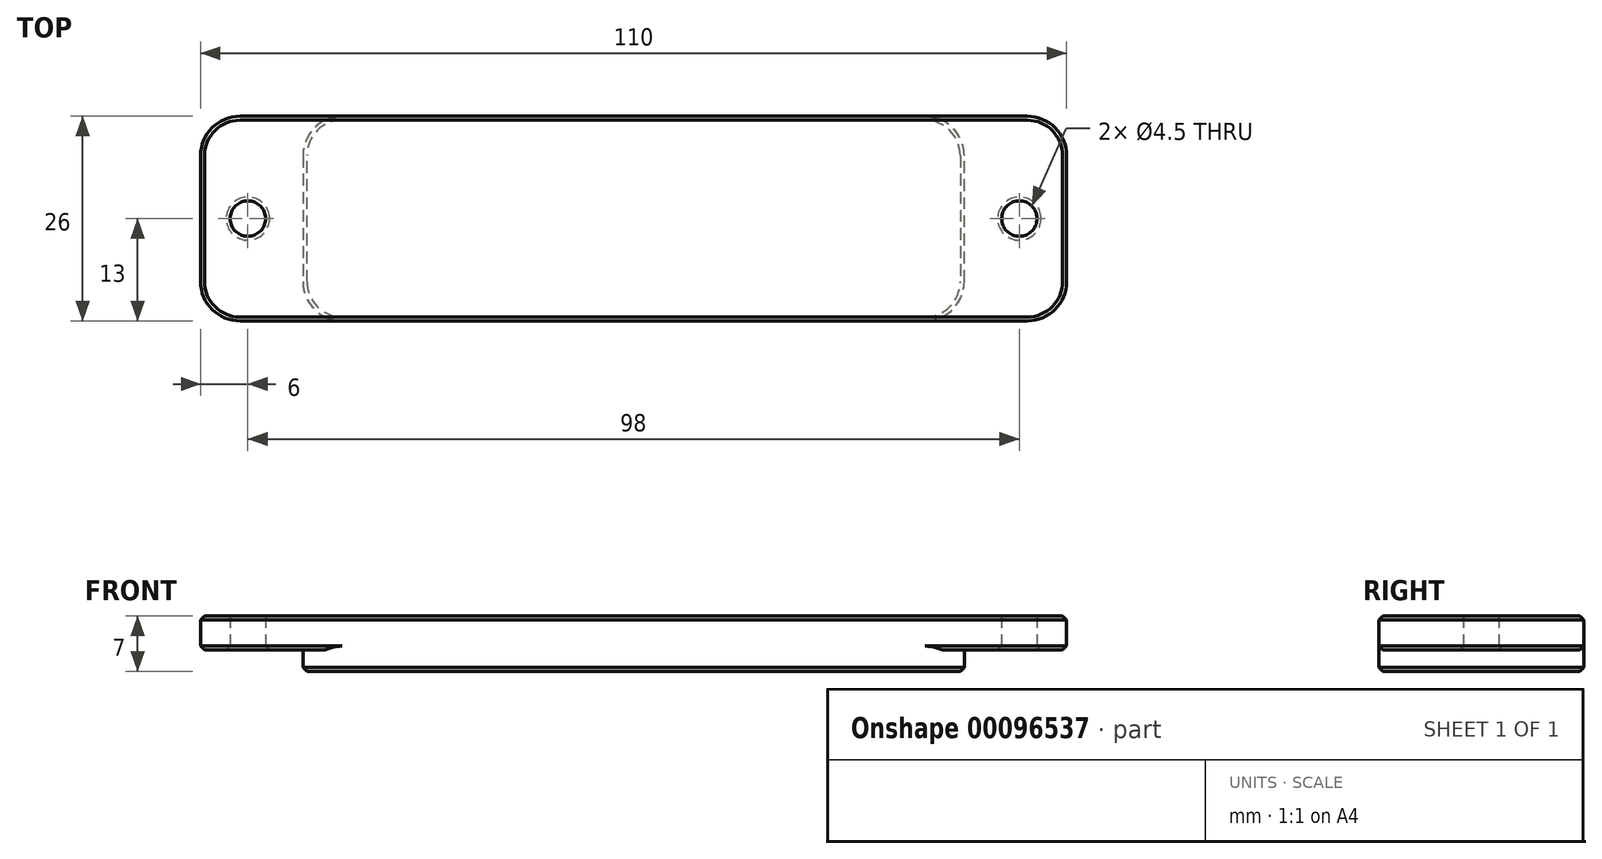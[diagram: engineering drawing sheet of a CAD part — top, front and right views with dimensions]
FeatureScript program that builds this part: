
annotation { "Feature Type Name" : "Feature", "Feature Type Description" : "" }
export const myFeature = defineFeature(function(context is Context, id is Id, definition is map)
    precondition{}
    {
        {
            var Q0;
            Q0=qCreatedBy(makeId("Top.planeOp"),FACE);
            var sketch = newSketch(context, id + "F0", { "sketchPlane" : qUnion([Q0])});
            skLineSegment(sketch, "E0.bottom", {"start": v(-37, 13) * mm, "end": v(37, 13) * mm});
            skLineSegment(sketch, "E0.top", {"start": v(-37, -13) * mm, "end": v(37, -13) * mm});
            skLineSegment(sketch, "E0.left", {"start": v(-42, 8) * mm, "end": v(-42, -8) * mm});
            skLineSegment(sketch, "E0.right", {"start": v(42, 8) * mm, "end": v(42, -8) * mm});
            skPoint(sketch, "E0.middle", {"position": v(0, 0) * mm});
            skPoint(sketch, "E1.visualSharp", {"position": v(-42, 13) * mm});
            skArc(sketch, "E1.filletArc", {"start": v(-37, 13) * mm, "mid": v(-40.54, 11.54) * mm, "end": v(-42, 8) * mm});
            skPoint(sketch, "E2.visualSharp", {"position": v(42, 13) * mm});
            skArc(sketch, "E2.filletArc", {"start": v(42, 8) * mm, "mid": v(40.54, 11.54) * mm, "end": v(37, 13) * mm});
            skPoint(sketch, "E3.visualSharp", {"position": v(42, -13) * mm});
            skArc(sketch, "E3.filletArc", {"start": v(37, -13) * mm, "mid": v(40.54, -11.54) * mm, "end": v(42, -8) * mm});
            skPoint(sketch, "E4.visualSharp", {"position": v(-42, -13) * mm});
            skArc(sketch, "E4.filletArc", {"start": v(-42, -8) * mm, "mid": v(-40.54, -11.54) * mm, "end": v(-37, -13) * mm});
            skSolve(sketch);
        }
        {
            var Q0;
            Q0 = qSketchRegion(id + "F0", true);
            extrude(context, id + "F1", {"entities" : qUnion([Q0]), "depth" : 2.7 * mm, "offsetDistance" : 25 * mm});
        }
        {
            var Q0;
            Q0=makeQuery(id+"F1.opExtrude","CAP_FACE",FACE,{"disambiguationData":[OSD([sQuery(id+"F0.wireOp",EDGE,"E0.bottom"),sQuery(id+"F0.wireOp",EDGE,"E0.top"),sQuery(id+"F0.wireOp",EDGE,"E0.left"),sQuery(id+"F0.wireOp",EDGE,"E0.right"),sQuery(id+"F0.wireOp",EDGE,"E1.filletArc"),sQuery(id+"F0.wireOp",EDGE,"E2.filletArc"),sQuery(id+"F0.wireOp",EDGE,"E3.filletArc"),sQuery(id+"F0.wireOp",EDGE,"E4.filletArc")])],"isStart":true});
            cPlane(context, id + "F2", {"entities" : qUnion([Q0]), "cplaneType" : CPlaneType.OFFSET, "offset" : 7 * mm, "oppositeDirection" : true, "width" : 150 * mm, "height" : 150 * mm});
        }
        {
            var Q0;
            Q0=makeQuery(id+"F1.opExtrude","CAP_FACE",FACE,{"disambiguationData":[OSD([sQuery(id+"F0.wireOp",EDGE,"E0.bottom"),sQuery(id+"F0.wireOp",EDGE,"E0.top"),sQuery(id+"F0.wireOp",EDGE,"E0.left"),sQuery(id+"F0.wireOp",EDGE,"E0.right"),sQuery(id+"F0.wireOp",EDGE,"E1.filletArc"),sQuery(id+"F0.wireOp",EDGE,"E2.filletArc"),sQuery(id+"F0.wireOp",EDGE,"E3.filletArc"),sQuery(id+"F0.wireOp",EDGE,"E4.filletArc")])],"isStart":false});
            var sketch = newSketch(context, id + "F3", { "sketchPlane" : qUnion([Q0])});
            skPoint(sketch, "E5.middle", {"position": v(0, 0) * mm});
            skPoint(sketch, "E6.orphan", {"position": v(-37, -13) * mm});
            skPoint(sketch, "E7.orphan", {"position": v(37, -13) * mm});
            skPoint(sketch, "E8.orphan", {"position": v(37, 13) * mm});
            skPoint(sketch, "E9.orphan", {"position": v(-37, 13) * mm});
            skLineSegment(sketch, "E10.bottom", {"start": v(-50, 13) * mm, "end": v(50, 13) * mm});
            skLineSegment(sketch, "E10.top", {"start": v(-50, -13) * mm, "end": v(50, -13) * mm});
            skLineSegment(sketch, "E10.left", {"start": v(-55, 8) * mm, "end": v(-55, -8) * mm});
            skLineSegment(sketch, "E10.right", {"start": v(55, 8) * mm, "end": v(55, -8) * mm});
            skPoint(sketch, "E11.visualSharp", {"position": v(-55, 13) * mm});
            skArc(sketch, "E11.filletArc", {"start": v(-50, 13) * mm, "mid": v(-53.54, 11.54) * mm, "end": v(-55, 8) * mm});
            skPoint(sketch, "E12.visualSharp", {"position": v(55, 13) * mm});
            skArc(sketch, "E12.filletArc", {"start": v(55, 8) * mm, "mid": v(53.54, 11.54) * mm, "end": v(50, 13) * mm});
            skPoint(sketch, "E13.visualSharp", {"position": v(55, -13) * mm});
            skArc(sketch, "E13.filletArc", {"start": v(50, -13) * mm, "mid": v(53.54, -11.54) * mm, "end": v(55, -8) * mm});
            skPoint(sketch, "E14.visualSharp", {"position": v(-55, -13) * mm});
            skArc(sketch, "E14.filletArc", {"start": v(-55, -8) * mm, "mid": v(-53.54, -11.54) * mm, "end": v(-50, -13) * mm});
            skCircle(sketch, "E15", {"center": v(-49, 0) * mm, "radius": 2.25 * mm});
            skCircle(sketch, "E16", {"center": v(49, 0) * mm, "radius": 2.25 * mm});
            skArc(sketch, "E17.0.0", {"start": v(-42, -8) * mm, "mid": v(-40.54, -11.54) * mm, "end": v(-37, -13) * mm, "construction": true});
            skLineSegment(sketch, "E17.0.1", {"start": v(-37, -13) * mm, "end": v(37, -13) * mm, "construction": true});
            skArc(sketch, "E17.0.2", {"start": v(37, -13) * mm, "mid": v(40.54, -11.54) * mm, "end": v(42, -8) * mm, "construction": true});
            skLineSegment(sketch, "E17.0.3", {"start": v(42, -8) * mm, "end": v(42, 8) * mm, "construction": true});
            skArc(sketch, "E17.0.4", {"start": v(42, 8) * mm, "mid": v(40.54, 11.54) * mm, "end": v(37, 13) * mm, "construction": true});
            skLineSegment(sketch, "E17.0.5", {"start": v(37, 13) * mm, "end": v(-37, 13) * mm, "construction": true});
            skArc(sketch, "E17.0.6", {"start": v(-37, 13) * mm, "mid": v(-40.54, 11.54) * mm, "end": v(-42, 8) * mm, "construction": true});
            skLineSegment(sketch, "E17.0.7", {"start": v(-42, 8) * mm, "end": v(-42, -8) * mm, "construction": true});
            skSolve(sketch);
        }
        {
            var Q0;
            Q0=makeQuery(id+"F3.imprint","IMPRINT",FACE,{"disambiguationData":[TD([[makeQuery(id+"F3.imprint","IMPRINT",EDGE,{"derivedFrom":sQuery(id+"F3.wireOp",EDGE,"E10.bottom")}),-1.0]])]});
            var Q1;
            Q1=makeQuery(id+"F3.imprint","IMPRINT",FACE,{"disambiguationData":[TD([[makeQuery(id+"F3.imprint","IMPRINT",EDGE,{"derivedFrom":sQuery(id+"F3.wireOp",EDGE,"E10.right")}),-1.0]])]});
            var Q2;
            Q2=makeQuery(id+"F3.imprint","IMPRINT",FACE,{"disambiguationData":[TD([[makeQuery(id+"F3.imprint","IMPRINT",EDGE,{"derivedFrom":sQuery(id+"F3.wireOp",EDGE,"E10.left")}),1.0]])]});
            var Q3;
            Q3=qCreatedBy(id+"F2.planeOp",FACE);
            extrude(context, id + "F4", {"entities" : qUnion([Q0, Q1, Q2]), "operationType" : NewBodyOperationType.ADD, "endBound" : BoundingType.UP_TO_SURFACE, "depth" : 2.5 * mm, "endBoundEntityFace" : qUnion([Q3]), "offsetDistance" : 25 * mm});
        }
        {
            var Q0;
            Q0=makeQuery(id+"F1.opExtrude","CAP_EDGE",EDGE,{"disambiguationData":[OSD([sQuery(id+"F0.wireOp",EDGE,"E0.top")])],"isStart":true});
            var Q1;
            Q1=makeQuery(id+"F4.opExtrude","CAP_EDGE",EDGE,{"disambiguationData":[OSD([sQuery(id+"F3.wireOp",EDGE,"E16")])],"isStart":true});
            var Q2;
            Q2=makeQuery(id+"F4.opExtrude","CAP_EDGE",EDGE,{"disambiguationData":[OSD([sQuery(id+"F3.wireOp",EDGE,"E15")])],"isStart":true});
            var Q3;
            {var subQ0=sQuery(id+"F3.wireOp",EDGE,"E10.bottom");Q3=makeQuery(id+"F4.boolean.opBoolean","SPLIT",EDGE,{"disambiguationData":[TD([makeQuery(id+"F1.opExtrude","SWEPT_FACE",FACE,{"disambiguationData":[OSD([sQuery(id+"F0.wireOp",EDGE,"E1.filletArc")])]})])],"derivedFrom":makeQuery(id+"F4.opExtrude","CAP_EDGE",EDGE,{"disambiguationData":[OSD([subQ0])],"isStart":true})});}
            var Q4;
            {var subQ0=sQuery(id+"F3.wireOp",EDGE,"E10.bottom");Q4=makeQuery(id+"F4.boolean.opBoolean","SPLIT",EDGE,{"disambiguationData":[TD([makeQuery(id+"F1.opExtrude","SWEPT_FACE",FACE,{"disambiguationData":[OSD([sQuery(id+"F0.wireOp",EDGE,"E2.filletArc")])]})])],"derivedFrom":makeQuery(id+"F4.opExtrude","CAP_EDGE",EDGE,{"disambiguationData":[OSD([subQ0])],"isStart":true})});}
            var Q5;
            Q5=makeQuery(id+"F4.opExtrude","CAP_EDGE",EDGE,{"disambiguationData":[OSD([sQuery(id+"F3.wireOp",EDGE,"E10.bottom")])],"isStart":false});
            chamfer(context, id + "F5", {"entities" : qUnion([Q0, Q1, Q2, Q3, Q4, Q5]), "width" : .5 * mm, "tangentPropagation" : true});
        }
    });
